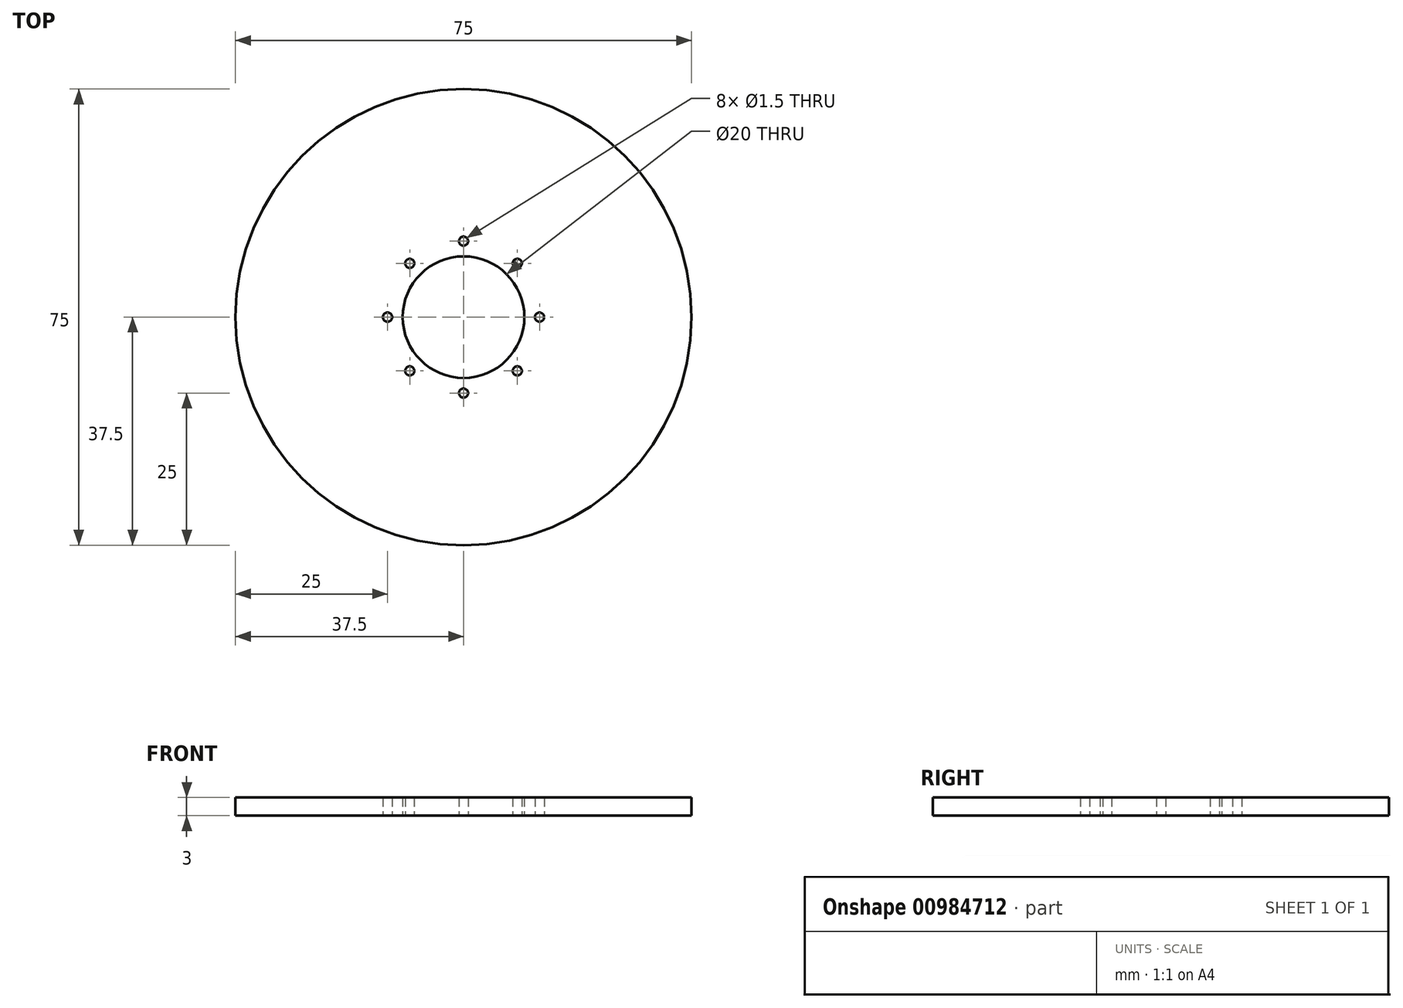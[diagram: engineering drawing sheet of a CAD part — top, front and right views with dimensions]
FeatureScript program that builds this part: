
annotation { "Feature Type Name" : "Feature", "Feature Type Description" : "" }
export const myFeature = defineFeature(function(context is Context, id is Id, definition is map)
    precondition{}
    {
        {
            var Q0;
            Q0=qCreatedBy(makeId("Top.planeOp"),FACE);
            var sketch = newSketch(context, id + "F0", { "sketchPlane" : qUnion([Q0])});
            skCircle(sketch, "E0", {"center": v(0, 0) * mm, "radius": 37.5 * mm});
            skSolve(sketch);
        }
        {
            var Q0;
            Q0=qCreatedBy(makeId("Top.planeOp"),FACE);
            var sketch = newSketch(context, id + "F1", { "sketchPlane" : qUnion([Q0])});
            skCircle(sketch, "E1", {"center": v(0, 0) * mm, "radius": 12.5 * mm, "construction": true});
            skLineSegment(sketch, "E2", {"start": v(0, 37.5) * mm, "end": v(0, -37.5) * mm, "construction": true});
            skLineSegment(sketch, "E3", {"start": v(-37.5, 0) * mm, "end": v(37.5, 0) * mm, "construction": true});
            skLineSegment(sketch, "E4", {"start": v(-26.52, -26.52) * mm, "end": v(26.52, 26.52) * mm, "construction": true});
            skLineSegment(sketch, "E5", {"start": v(26.52, -26.52) * mm, "end": v(-26.52, 26.52) * mm, "construction": true});
            skSolve(sketch);
        }
        {
            var Q0;
            Q0=qCreatedBy(makeId("Top.planeOp"),FACE);
            var sketch = newSketch(context, id + "F2", { "sketchPlane" : qUnion([Q0])});
            skCircle(sketch, "E6", {"center": v(0, 0) * mm, "radius": 10 * mm});
            skSolve(sketch);
        }
        {
            var Q0;
            Q0=qCreatedBy(makeId("Top.planeOp"),FACE);
            var sketch = newSketch(context, id + "F3", { "sketchPlane" : qUnion([Q0])});
            skCircle(sketch, "E7", {"center": v(-8.84, 8.84) * mm, "radius": 0.75 * mm});
            skCircle(sketch, "E8", {"center": v(0, 12.5) * mm, "radius": 0.75 * mm});
            skCircle(sketch, "E9", {"center": v(8.84, 8.84) * mm, "radius": 0.75 * mm});
            skCircle(sketch, "E10", {"center": v(12.5, 0) * mm, "radius": 0.75 * mm});
            skCircle(sketch, "E11", {"center": v(8.84, -8.84) * mm, "radius": 0.75 * mm});
            skCircle(sketch, "E12", {"center": v(0, -12.5) * mm, "radius": 0.75 * mm});
            skCircle(sketch, "E13", {"center": v(-8.84, -8.84) * mm, "radius": 0.75 * mm});
            skCircle(sketch, "E14", {"center": v(-12.5, 0) * mm, "radius": 0.75 * mm});
            skSolve(sketch);
        }
        {
            var Q0;
            Q0=makeQuery(id+"F0.imprint","IMPRINT",FACE,{"disambiguationData":[TD([[makeQuery(id+"F0.imprint","IMPRINT",EDGE,{"derivedFrom":sQuery(id+"F0.wireOp",EDGE,"E0")}),1.0]])]});
            extrude(context, id + "F4", {"entities" : qUnion([Q0]), "depth" : 3 * mm, "offsetDistance" : 25 * mm});
        }
        {
            var Q0;
            Q0 = qSketchRegion(id + "F2", true);
            var Q1;
            Q1 = qSketchRegion(id + "F3", true);
            extrude(context, id + "F5", {"entities" : qUnion([Q0, Q1]), "depth" : 3 * mm, "offsetDistance" : 25 * mm});
        }
        {
            var Q0;
            Q0=makeQuery(id+"F5.opExtrude","SWEPT_BODY",BODY,{"disambiguationData":[OSD([sQuery(id+"F2.wireOp",EDGE,"E6")])]});
            var Q1;
            Q1=makeQuery(id+"F5.opExtrude","SWEPT_BODY",BODY,{"disambiguationData":[OSD([sQuery(id+"F3.wireOp",EDGE,"E7")])]});
            var Q2;
            Q2=makeQuery(id+"F5.opExtrude","SWEPT_BODY",BODY,{"disambiguationData":[OSD([sQuery(id+"F3.wireOp",EDGE,"E8")])]});
            var Q3;
            Q3=makeQuery(id+"F5.opExtrude","SWEPT_BODY",BODY,{"disambiguationData":[OSD([sQuery(id+"F3.wireOp",EDGE,"E9")])]});
            var Q4;
            Q4=makeQuery(id+"F5.opExtrude","SWEPT_BODY",BODY,{"disambiguationData":[OSD([sQuery(id+"F3.wireOp",EDGE,"E10")])]});
            var Q5;
            Q5=makeQuery(id+"F5.opExtrude","SWEPT_BODY",BODY,{"disambiguationData":[OSD([sQuery(id+"F3.wireOp",EDGE,"E11")])]});
            var Q6;
            Q6=makeQuery(id+"F5.opExtrude","SWEPT_BODY",BODY,{"disambiguationData":[OSD([sQuery(id+"F3.wireOp",EDGE,"E12")])]});
            var Q7;
            Q7=makeQuery(id+"F5.opExtrude","SWEPT_BODY",BODY,{"disambiguationData":[OSD([sQuery(id+"F3.wireOp",EDGE,"E13")])]});
            var Q8;
            Q8=makeQuery(id+"F5.opExtrude","SWEPT_BODY",BODY,{"disambiguationData":[OSD([sQuery(id+"F3.wireOp",EDGE,"E14")])]});
            var Q9;
            Q9=makeQuery(id+"F4.opExtrude","SWEPT_BODY",BODY,{"disambiguationData":[OSD([sQuery(id+"F0.wireOp",EDGE,"E0")])]});
            booleanBodies(context, id + "F6", {"operationType" : BooleanOperationType.SUBTRACTION, "tools" : qUnion([Q0, Q1, Q2, Q3, Q4, Q5, Q6, Q7, Q8]), "targets" : qUnion([Q9])});
        }
    });
